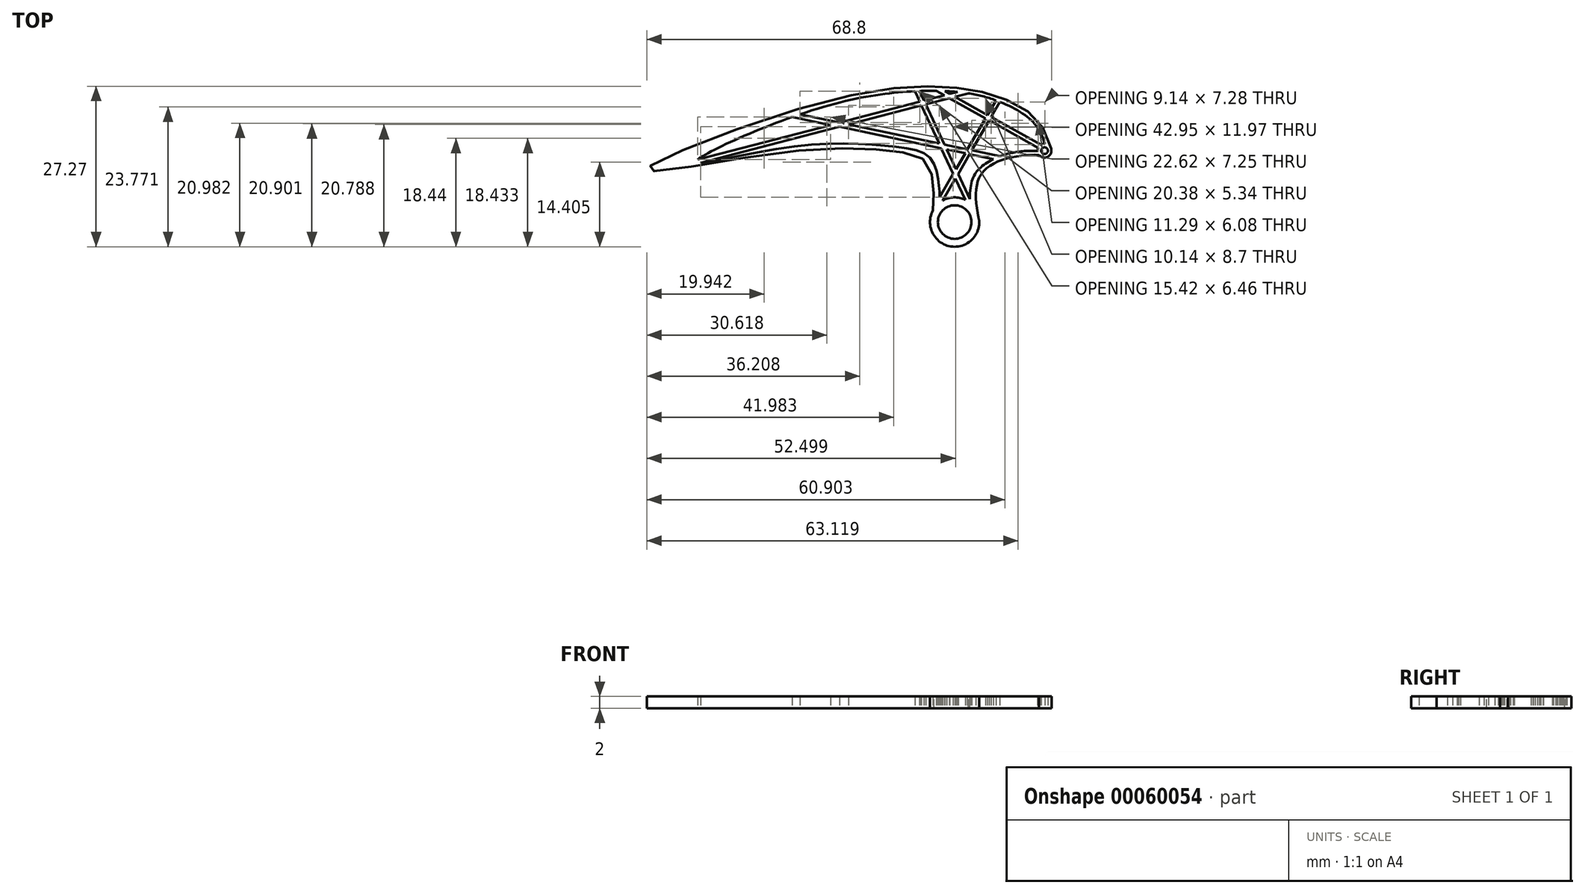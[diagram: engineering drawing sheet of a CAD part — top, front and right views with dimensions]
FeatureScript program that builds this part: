
annotation { "Feature Type Name" : "Feature", "Feature Type Description" : "" }
export const myFeature = defineFeature(function(context is Context, id is Id, definition is map)
    precondition{}
    {
        {
            var Q0;
            Q0=qCreatedBy(makeId("Top.planeOp"),FACE);
            var sketch = newSketch(context, id + "F0", { "sketchPlane" : qUnion([Q0])});
            skCircle(sketch, "E0", {"center": v(22.3, -8.9) * mm, "radius": 2.86 * mm});
            skCircle(sketch, "E1", {"center": v(22.3, -8.9) * mm, "radius": 4.2 * mm});
            skCircle(sketch, "E2", {"center": v(37.58, 3.23) * mm, "radius": 0.57 * mm});
            skCircle(sketch, "E3", {"center": v(37.58, 3.23) * mm, "radius": 1.18 * mm});
            skFitSpline(sketch, "E4", {"points": [v(26.49, -8.74) * mm, v(27.46, 0) * mm, v(36.65, 2.52) * mm], "startDerivative": vector(-5.2, 22.22) * mm, "endDerivative": vector(16.24, -0.78) * mm});
            skFitSpline(sketch, "E5", {"points": [v(18.61, -6.9) * mm, v(18.72, -2.98) * mm, v(17.38, 1.38) * mm, v(11.85, 3.14) * mm, v(-6.78, 2.97) * mm, v(-30.04, 0) * mm, v(-1.5, 11.11) * mm, v(19.9, 14.13) * mm, v(28.88, 12.7) * mm, v(35.67, 9.1) * mm, v(38.75, 3.39) * mm], "startDerivative": vector(5.07, 64.8) * mm, "endDerivative": vector(19.44, -96.7) * mm});
            skFitSpline(sketch, "E6", {"points": [v(19.7, -5.62) * mm, v(19.6, -2.67) * mm, v(18.27, 1.82) * mm, v(12.1, 3.9) * mm, v(-6.7, 3.73) * mm, v(-21.73, 1.29) * mm, v(-1.28, 10.3) * mm, v(19.83, 13.37) * mm, v(28.58, 12.04) * mm, v(35.2, 8.53) * mm, v(37.65, 4.4) * mm], "startDerivative": vector(6.6, 64.66) * mm, "endDerivative": vector(29.19, -84.57) * mm});
            skFitSpline(sketch, "E7", {"points": [v(24.9, -5.61) * mm, v(26.9, 0.53) * mm, v(36.4, 3.2) * mm], "startDerivative": vector(-0.66, 23.1) * mm, "endDerivative": vector(24.75, -0.76) * mm});
            skLineSegment(sketch, "E8", {"start": v(20.27, -5.24) * mm, "end": v(30, 11.52) * mm});
            skLineSegment(sketch, "E9", {"start": v(19.75, -4.68) * mm, "end": v(29.3, 11.79) * mm});
            skLineSegment(sketch, "E10", {"start": v(24.1, -5.12) * mm, "end": v(15.52, 13.34) * mm});
            skLineSegment(sketch, "E11", {"start": v(24.88, -5.01) * mm, "end": v(16.34, 13.37) * mm});
            skLineSegment(sketch, "E12", {"start": v(-20.9, 1.14) * mm, "end": v(24.6, 12.99) * mm});
            skLineSegment(sketch, "E13", {"start": v(-21.4, 1.71) * mm, "end": v(22.76, 13.21) * mm});
            skLineSegment(sketch, "E14", {"start": v(36.5, 3.72) * mm, "end": v(19.18, 13.39) * mm});
            skLineSegment(sketch, "E15", {"start": v(36.97, 4.24) * mm, "end": v(20.65, 13.35) * mm});
            skLineSegment(sketch, "E16", {"start": v(28.86, 1.8) * mm, "end": v(-5.31, 8.97) * mm});
            skLineSegment(sketch, "E17", {"start": v(-4.02, 9.42) * mm, "end": v(30, 2.3) * mm});
            skSolve(sketch);
        }
        {
            var Q0;
            Q0=makeQuery(id+"F0.imprint","IMPRINT",FACE,{"disambiguationData":[TD([[makeQuery(id+"F0.imprint","IMPRINT",EDGE,{"derivedFrom":sQuery(id+"F0.wireOp",EDGE,"E0")}),-1.0]])]});
            var Q1;
            {var subQ0=sQuery(id+"F0.wireOp",EDGE,"E5");var subQ1=sQuery(id+"F0.wireOp",EDGE,"E1");var subQ2=makeQuery(id+"F0.imprint","INTERSECT",VERTEX,{"derivedFrom":[subQ1,subQ0]});Q1=makeQuery(id+"F0.imprint","IMPRINT",FACE,{"disambiguationData":[TD([[makeQuery(id+"F0.imprint","IMPRINT",EDGE,{"disambiguationData":[TD([[subQ2,1.0]])],"derivedFrom":subQ1}),-1.0]])]});}
            var Q2;
            Q2=makeQuery(id+"F0.imprint","IMPRINT",FACE,{"disambiguationData":[TD([[makeQuery(id+"F0.imprint","IMPRINT",EDGE,{"derivedFrom":sQuery(id+"F0.wireOp",EDGE,"E2")}),-1.0]])]});
            var Q3;
            {var subQ0=sQuery(id+"F0.wireOp",EDGE,"E7");Q3=makeQuery(id+"F0.imprint","IMPRINT",FACE,{"disambiguationData":[TD([[makeQuery(id+"F0.imprint","IMPRINT",EDGE,{"derivedFrom":subQ0}),-1.0]])]});}
            var Q4;
            {var subQ1=sQuery(id+"F0.wireOp",EDGE,"E6");var subQ7=sQuery(id+"F0.wireOp",EDGE,"E1");var subQ9=makeQuery(id+"F0.imprint","INTERSECT",VERTEX,{"derivedFrom":[subQ7,subQ1]});Q4=makeQuery(id+"F0.imprint","IMPRINT",FACE,{"disambiguationData":[TD([[makeQuery(id+"F0.imprint","IMPRINT",EDGE,{"disambiguationData":[TD([[subQ9,1.0]])],"derivedFrom":subQ7}),-1.0]])]});}
            var Q5;
            {var subQ1=sQuery(id+"F0.wireOp",EDGE,"E1");var subQ7=sQuery(id+"F0.wireOp",EDGE,"E7");var subQ8=makeQuery(id+"F0.imprint","INTERSECT",VERTEX,{"derivedFrom":[subQ1,subQ7]});Q5=makeQuery(id+"F0.imprint","IMPRINT",FACE,{"disambiguationData":[TD([[makeQuery(id+"F0.imprint","IMPRINT",EDGE,{"disambiguationData":[TD([[subQ8,-1.0]])],"derivedFrom":subQ1}),-1.0]])]});}
            var Q6;
            {var subQ0=sQuery(id+"F0.wireOp",EDGE,"E10");var subQ1=sQuery(id+"F0.wireOp",EDGE,"E8");var subQ2=makeQuery(id+"F0.imprint","INTERSECT",VERTEX,{"derivedFrom":[subQ1,subQ0]});Q6=makeQuery(id+"F0.imprint","IMPRINT",FACE,{"disambiguationData":[TD([[makeQuery(id+"F0.imprint","IMPRINT",EDGE,{"disambiguationData":[TD([[subQ2,-1.0]])],"derivedFrom":subQ1}),1.0]])]});}
            var Q7;
            {var subQ0=sQuery(id+"F0.wireOp",EDGE,"E11");var subQ1=sQuery(id+"F0.wireOp",EDGE,"E8");var subQ2=makeQuery(id+"F0.imprint","INTERSECT",VERTEX,{"derivedFrom":[subQ1,subQ0]});Q7=makeQuery(id+"F0.imprint","IMPRINT",FACE,{"disambiguationData":[TD([[makeQuery(id+"F0.imprint","IMPRINT",EDGE,{"disambiguationData":[TD([[subQ2,-1.0]])],"derivedFrom":subQ1}),1.0]])]});}
            var Q8;
            {var subQ0=sQuery(id+"F0.wireOp",EDGE,"E14");var subQ1=sQuery(id+"F0.wireOp",EDGE,"E3");var subQ2=makeQuery(id+"F0.imprint","INTERSECT",VERTEX,{"derivedFrom":[subQ1,subQ0]});Q8=makeQuery(id+"F0.imprint","IMPRINT",FACE,{"disambiguationData":[TD([[makeQuery(id+"F0.imprint","IMPRINT",EDGE,{"disambiguationData":[TD([[subQ2,1.0]])],"derivedFrom":subQ1}),-1.0]])]});}
            var Q9;
            {var subQ0=sQuery(id+"F0.wireOp",EDGE,"E14");var subQ1=sQuery(id+"F0.wireOp",EDGE,"E8");var subQ2=makeQuery(id+"F0.imprint","INTERSECT",VERTEX,{"derivedFrom":[subQ1,subQ0]});Q9=makeQuery(id+"F0.imprint","IMPRINT",FACE,{"disambiguationData":[TD([[makeQuery(id+"F0.imprint","IMPRINT",EDGE,{"disambiguationData":[TD([[subQ2,-1.0]])],"derivedFrom":subQ1}),1.0]])]});}
            var Q10;
            {var subQ0=sQuery(id+"F0.wireOp",EDGE,"E8");var subQ1=sQuery(id+"F0.wireOp",EDGE,"E6");var subQ2=makeQuery(id+"F0.imprint","INTERSECT",VERTEX,{"derivedFrom":[subQ1,subQ0]});Q10=makeQuery(id+"F0.imprint","IMPRINT",FACE,{"disambiguationData":[TD([[makeQuery(id+"F0.imprint","IMPRINT",EDGE,{"disambiguationData":[TD([[subQ2,1.0]])],"derivedFrom":subQ1}),-1.0]])]});}
            var Q11;
            {var subQ0=sQuery(id+"F0.wireOp",EDGE,"E14");var subQ1=sQuery(id+"F0.wireOp",EDGE,"E9");var subQ2=makeQuery(id+"F0.imprint","INTERSECT",VERTEX,{"derivedFrom":[subQ1,subQ0]});Q11=makeQuery(id+"F0.imprint","IMPRINT",FACE,{"disambiguationData":[TD([[makeQuery(id+"F0.imprint","IMPRINT",EDGE,{"disambiguationData":[TD([[subQ2,-1.0]])],"derivedFrom":subQ1}),1.0]])]});}
            var Q12;
            {var subQ0=sQuery(id+"F0.wireOp",EDGE,"E10");var subQ1=sQuery(id+"F0.wireOp",EDGE,"E9");var subQ2=makeQuery(id+"F0.imprint","INTERSECT",VERTEX,{"derivedFrom":[subQ1,subQ0]});Q12=makeQuery(id+"F0.imprint","IMPRINT",FACE,{"disambiguationData":[TD([[makeQuery(id+"F0.imprint","IMPRINT",EDGE,{"disambiguationData":[TD([[subQ2,-1.0]])],"derivedFrom":subQ1}),1.0]])]});}
            var Q13;
            {var subQ0=sQuery(id+"F0.wireOp",EDGE,"E12");var subQ1=sQuery(id+"F0.wireOp",EDGE,"E11");var subQ2=makeQuery(id+"F0.imprint","INTERSECT",VERTEX,{"derivedFrom":[subQ1,subQ0]});Q13=makeQuery(id+"F0.imprint","IMPRINT",FACE,{"disambiguationData":[TD([[makeQuery(id+"F0.imprint","IMPRINT",EDGE,{"disambiguationData":[TD([[subQ2,-1.0]])],"derivedFrom":subQ1}),-1.0]])]});}
            var Q14;
            {var subQ0=sQuery(id+"F0.wireOp",EDGE,"E12");var subQ1=sQuery(id+"F0.wireOp",EDGE,"E6");var subQ2=makeQuery(id+"F0.imprint","INTERSECT",VERTEX,{"disambiguationData":[OD(1.0)],"derivedFrom":[subQ1,subQ0]});Q14=makeQuery(id+"F0.imprint","IMPRINT",FACE,{"disambiguationData":[TD([[makeQuery(id+"F0.imprint","IMPRINT",EDGE,{"disambiguationData":[TD([[subQ2,1.0]])],"derivedFrom":subQ1}),-1.0]])]});}
            var Q15;
            {var subQ0=sQuery(id+"F0.wireOp",EDGE,"E14");var subQ1=sQuery(id+"F0.wireOp",EDGE,"E12");var subQ2=makeQuery(id+"F0.imprint","INTERSECT",VERTEX,{"derivedFrom":[subQ1,subQ0]});Q15=makeQuery(id+"F0.imprint","IMPRINT",FACE,{"disambiguationData":[TD([[makeQuery(id+"F0.imprint","IMPRINT",EDGE,{"disambiguationData":[TD([[subQ2,-1.0]])],"derivedFrom":subQ1}),1.0]])]});}
            var Q16;
            {var subQ0=sQuery(id+"F0.wireOp",EDGE,"E14");var subQ1=sQuery(id+"F0.wireOp",EDGE,"E6");var subQ2=makeQuery(id+"F0.imprint","INTERSECT",VERTEX,{"derivedFrom":[subQ1,subQ0]});Q16=makeQuery(id+"F0.imprint","IMPRINT",FACE,{"disambiguationData":[TD([[makeQuery(id+"F0.imprint","IMPRINT",EDGE,{"disambiguationData":[TD([[subQ2,-1.0]])],"derivedFrom":subQ1}),-1.0]])]});}
            var Q17;
            {var subQ0=sQuery(id+"F0.wireOp",EDGE,"E12");var subQ1=sQuery(id+"F0.wireOp",EDGE,"E10");var subQ2=makeQuery(id+"F0.imprint","INTERSECT",VERTEX,{"derivedFrom":[subQ1,subQ0]});Q17=makeQuery(id+"F0.imprint","IMPRINT",FACE,{"disambiguationData":[TD([[makeQuery(id+"F0.imprint","IMPRINT",EDGE,{"disambiguationData":[TD([[subQ2,-1.0]])],"derivedFrom":subQ1}),-1.0]])]});}
            var Q18;
            {var subQ0=sQuery(id+"F0.wireOp",EDGE,"E10");var subQ1=sQuery(id+"F0.wireOp",EDGE,"E6");var subQ2=makeQuery(id+"F0.imprint","INTERSECT",VERTEX,{"derivedFrom":[subQ1,subQ0]});Q18=makeQuery(id+"F0.imprint","IMPRINT",FACE,{"disambiguationData":[TD([[makeQuery(id+"F0.imprint","IMPRINT",EDGE,{"disambiguationData":[TD([[subQ2,-1.0]])],"derivedFrom":subQ1}),-1.0]])]});}
            var Q19;
            {var subQ0=sQuery(id+"F0.wireOp",EDGE,"E12");var subQ1=sQuery(id+"F0.wireOp",EDGE,"E6");var subQ2=makeQuery(id+"F0.imprint","INTERSECT",VERTEX,{"disambiguationData":[OD(0.0)],"derivedFrom":[subQ1,subQ0]});Q19=makeQuery(id+"F0.imprint","IMPRINT",FACE,{"disambiguationData":[TD([[makeQuery(id+"F0.imprint","IMPRINT",EDGE,{"disambiguationData":[TD([[subQ2,-1.0]])],"derivedFrom":subQ1}),-1.0]])]});}
            var Q20;
            {var subQ0=sQuery(id+"F0.wireOp",EDGE,"E16");var subQ1=sQuery(id+"F0.wireOp",EDGE,"E10");var subQ2=makeQuery(id+"F0.imprint","INTERSECT",VERTEX,{"derivedFrom":[subQ1,subQ0]});Q20=makeQuery(id+"F0.imprint","IMPRINT",FACE,{"disambiguationData":[TD([[makeQuery(id+"F0.imprint","IMPRINT",EDGE,{"disambiguationData":[TD([[subQ2,-1.0]])],"derivedFrom":subQ1}),1.0]])]});}
            var Q21;
            {var subQ0=sQuery(id+"F0.wireOp",EDGE,"E12");var subQ1=sQuery(id+"F0.wireOp",EDGE,"E10");var subQ2=makeQuery(id+"F0.imprint","INTERSECT",VERTEX,{"derivedFrom":[subQ1,subQ0]});Q21=makeQuery(id+"F0.imprint","IMPRINT",FACE,{"disambiguationData":[TD([[makeQuery(id+"F0.imprint","IMPRINT",EDGE,{"disambiguationData":[TD([[subQ2,-1.0]])],"derivedFrom":subQ1}),1.0]])]});}
            var Q22;
            {var subQ0=sQuery(id+"F0.wireOp",EDGE,"E16");var subQ1=sQuery(id+"F0.wireOp",EDGE,"E6");var subQ2=makeQuery(id+"F0.imprint","INTERSECT",VERTEX,{"derivedFrom":[subQ1,subQ0]});Q22=makeQuery(id+"F0.imprint","IMPRINT",FACE,{"disambiguationData":[TD([[makeQuery(id+"F0.imprint","IMPRINT",EDGE,{"disambiguationData":[TD([[subQ2,-1.0]])],"derivedFrom":subQ1}),-1.0]])]});}
            var Q23;
            {var subQ0=sQuery(id+"F0.wireOp",EDGE,"E17");var subQ1=sQuery(id+"F0.wireOp",EDGE,"E10");var subQ2=makeQuery(id+"F0.imprint","INTERSECT",VERTEX,{"derivedFrom":[subQ1,subQ0]});Q23=makeQuery(id+"F0.imprint","IMPRINT",FACE,{"disambiguationData":[TD([[makeQuery(id+"F0.imprint","IMPRINT",EDGE,{"disambiguationData":[TD([[subQ2,-1.0]])],"derivedFrom":subQ1}),-1.0]])]});}
            var Q24;
            {var subQ0=sQuery(id+"F0.wireOp",EDGE,"E17");var subQ1=sQuery(id+"F0.wireOp",EDGE,"E8");var subQ2=makeQuery(id+"F0.imprint","INTERSECT",VERTEX,{"derivedFrom":[subQ1,subQ0]});Q24=makeQuery(id+"F0.imprint","IMPRINT",FACE,{"disambiguationData":[TD([[makeQuery(id+"F0.imprint","IMPRINT",EDGE,{"disambiguationData":[TD([[subQ2,-1.0]])],"derivedFrom":subQ1}),1.0]])]});}
            var Q25;
            {var subQ0=sQuery(id+"F0.wireOp",EDGE,"E16");var subQ1=sQuery(id+"F0.wireOp",EDGE,"E7");var subQ2=makeQuery(id+"F0.imprint","INTERSECT",VERTEX,{"derivedFrom":[subQ1,subQ0]});Q25=makeQuery(id+"F0.imprint","IMPRINT",FACE,{"disambiguationData":[TD([[makeQuery(id+"F0.imprint","IMPRINT",EDGE,{"disambiguationData":[TD([[subQ2,-1.0]])],"derivedFrom":subQ1}),1.0]])]});}
            var Q26;
            {var subQ0=sQuery(id+"F0.wireOp",EDGE,"E16");var subQ1=sQuery(id+"F0.wireOp",EDGE,"E9");var subQ2=makeQuery(id+"F0.imprint","INTERSECT",VERTEX,{"derivedFrom":[subQ1,subQ0]});Q26=makeQuery(id+"F0.imprint","IMPRINT",FACE,{"disambiguationData":[TD([[makeQuery(id+"F0.imprint","IMPRINT",EDGE,{"disambiguationData":[TD([[subQ2,-1.0]])],"derivedFrom":subQ1}),1.0]])]});}
            var Q27;
            {var subQ0=sQuery(id+"F0.wireOp",EDGE,"E16");var subQ1=sQuery(id+"F0.wireOp",EDGE,"E8");var subQ2=makeQuery(id+"F0.imprint","INTERSECT",VERTEX,{"derivedFrom":[subQ1,subQ0]});Q27=makeQuery(id+"F0.imprint","IMPRINT",FACE,{"disambiguationData":[TD([[makeQuery(id+"F0.imprint","IMPRINT",EDGE,{"disambiguationData":[TD([[subQ2,-1.0]])],"derivedFrom":subQ1}),1.0]])]});}
            var Q28;
            {var subQ0=sQuery(id+"F0.wireOp",EDGE,"E16");var subQ1=sQuery(id+"F0.wireOp",EDGE,"E10");var subQ2=makeQuery(id+"F0.imprint","INTERSECT",VERTEX,{"derivedFrom":[subQ1,subQ0]});Q28=makeQuery(id+"F0.imprint","IMPRINT",FACE,{"disambiguationData":[TD([[makeQuery(id+"F0.imprint","IMPRINT",EDGE,{"disambiguationData":[TD([[subQ2,-1.0]])],"derivedFrom":subQ1}),-1.0]])]});}
            var Q29;
            {var subQ0=sQuery(id+"F0.wireOp",EDGE,"E16");var subQ1=sQuery(id+"F0.wireOp",EDGE,"E12");var subQ2=makeQuery(id+"F0.imprint","INTERSECT",VERTEX,{"derivedFrom":[subQ1,subQ0]});Q29=makeQuery(id+"F0.imprint","IMPRINT",FACE,{"disambiguationData":[TD([[makeQuery(id+"F0.imprint","IMPRINT",EDGE,{"disambiguationData":[TD([[subQ2,-1.0]])],"derivedFrom":subQ1}),1.0]])]});}
            extrude(context, id + "F1", {"entities" : qUnion([Q0, Q1, Q2, Q3, Q4, Q5, Q6, Q7, Q8, Q9, Q10, Q11, Q12, Q13, Q14, Q15, Q16, Q17, Q18, Q19, Q20, Q21, Q22, Q23, Q24, Q25, Q26, Q27, Q28, Q29]), "depth" : 2 * mm});
        }
    });
